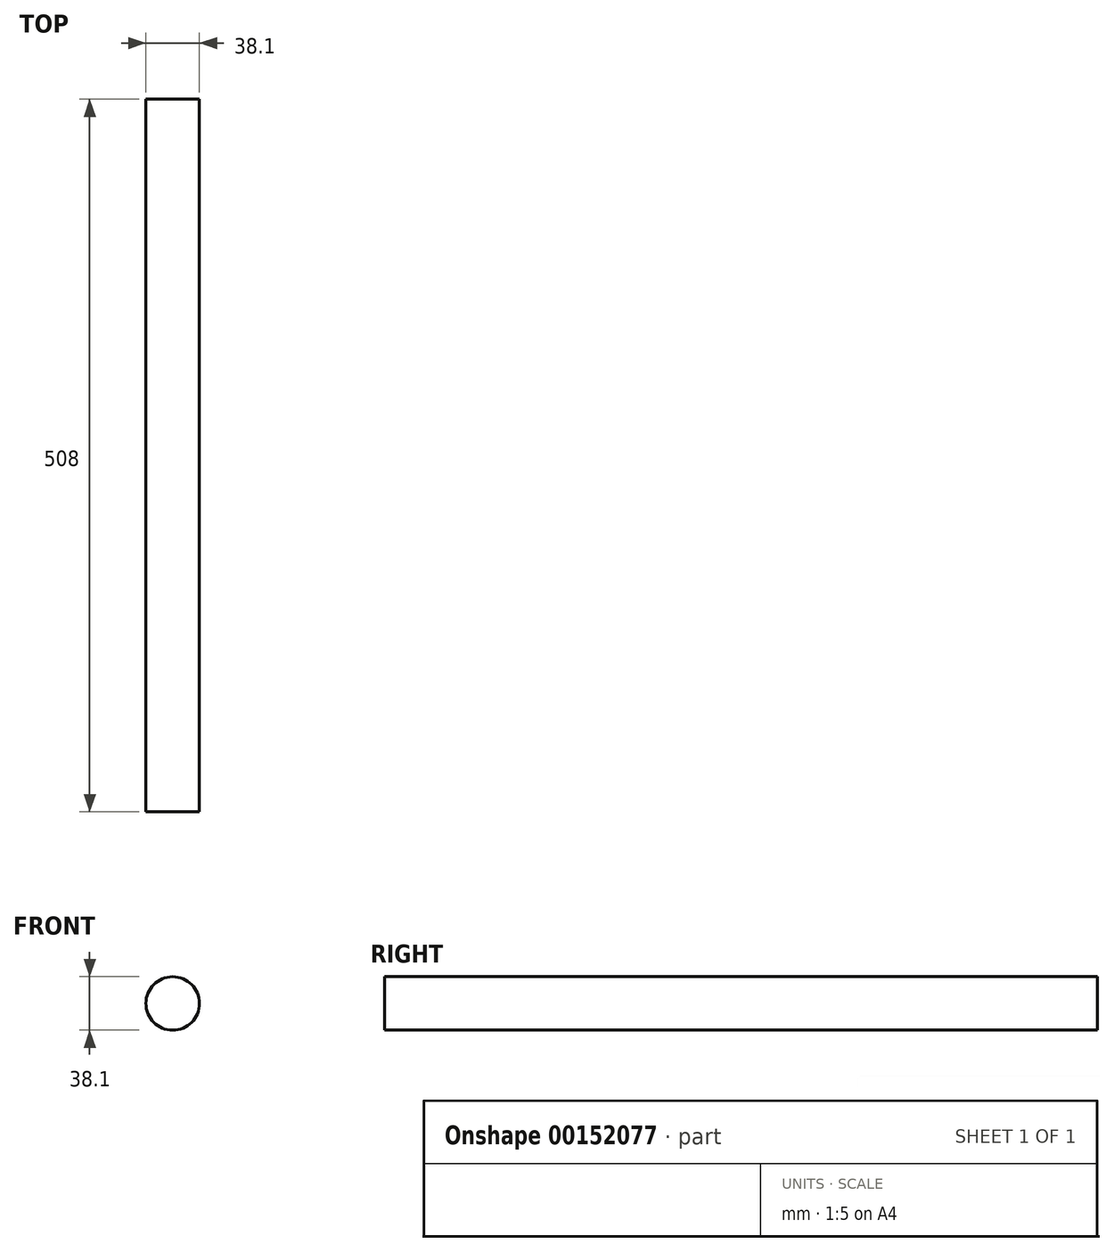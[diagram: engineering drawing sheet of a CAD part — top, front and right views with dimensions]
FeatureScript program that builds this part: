
annotation { "Feature Type Name" : "Feature", "Feature Type Description" : "" }
export const myFeature = defineFeature(function(context is Context, id is Id, definition is map)
    precondition{}
    {
        {
            var Q0;
            Q0=qCreatedBy(makeId("Front.planeOp"),FACE);
            var sketch = newSketch(context, id + "F0", { "sketchPlane" : qUnion([Q0])});
            skCircle(sketch, "E0", {"center": v(0, 0) * mm, "radius": 19.05 * mm});
            skSolve(sketch);
        }
        {
            var Q0;
            Q0 = qSketchRegion(id + "F0", true);
            extrude(context, id + "F1", {"entities" : qUnion([Q0]), "depth" : 508 * mm});
        }
    });
